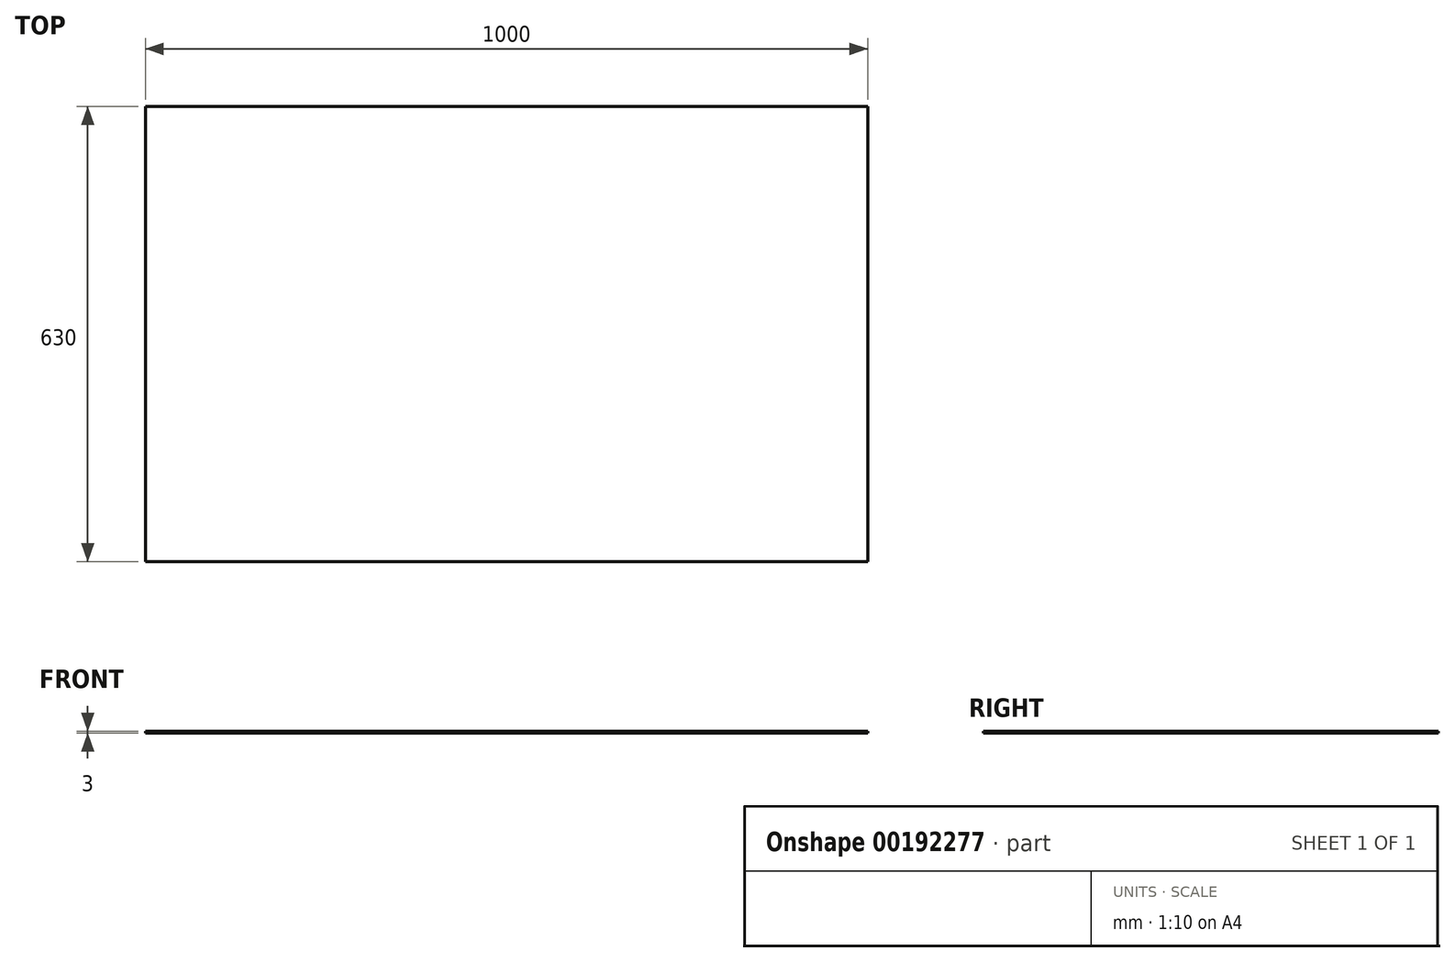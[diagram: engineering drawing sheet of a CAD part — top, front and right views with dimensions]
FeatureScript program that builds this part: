
annotation { "Feature Type Name" : "Feature", "Feature Type Description" : "" }
export const myFeature = defineFeature(function(context is Context, id is Id, definition is map)
    precondition{}
    {
        {
            var Q0;
            Q0=qCreatedBy(makeId("Top.planeOp"),FACE);
            var sketch = newSketch(context, id + "F0", { "sketchPlane" : qUnion([Q0])});
            skLineSegment(sketch, "E0.bottom", {"start": v(-496.2, -397.06) * mm, "end": v(503.8, -397.06) * mm});
            skLineSegment(sketch, "E0.top", {"start": v(-496.2, -1027.06) * mm, "end": v(503.8, -1027.06) * mm});
            skLineSegment(sketch, "E0.left", {"start": v(-496.2, -397.06) * mm, "end": v(-496.2, -1027.06) * mm});
            skLineSegment(sketch, "E0.right", {"start": v(503.8, -397.06) * mm, "end": v(503.8, -1027.06) * mm});
            skSolve(sketch);
        }
        {
            var Q0;
            Q0=makeQuery(id+"F0.imprint","IMPRINT",FACE,{"disambiguationData":[TD([[makeQuery(id+"F0.imprint","IMPRINT",EDGE,{"derivedFrom":sQuery(id+"F0.wireOp",EDGE,"E0.bottom")}),-1.0]])]});
            extrude(context, id + "F1", {"entities" : qUnion([Q0]), "depth" : 3 * mm, "offsetDistance" : 25 * mm});
        }
    });
